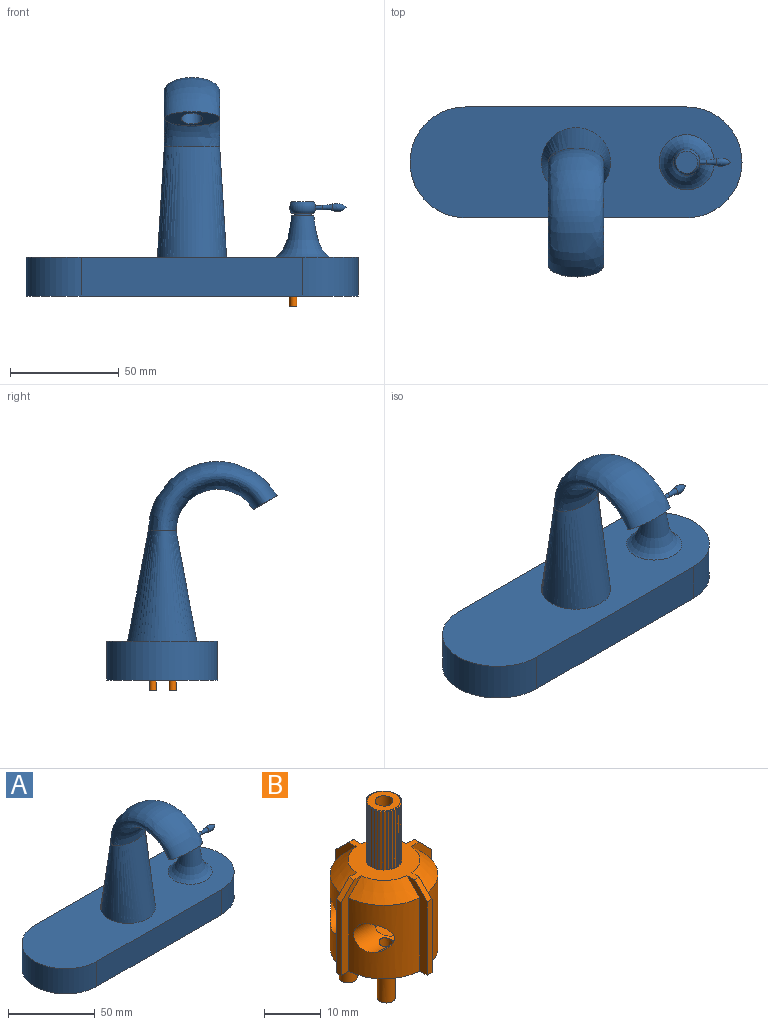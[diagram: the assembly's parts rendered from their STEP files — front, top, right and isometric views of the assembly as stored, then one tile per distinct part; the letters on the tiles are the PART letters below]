
ASSEMBLY  parts=2 mates=1
PART A: 38 faces, bbox 152.4x78.2x100.3 mm
  f0: plane 152.4x50.8mm, normal (0,0,1), area 5889.9mm2, adj f1,f2,f3,f4,f5,f13
  f1: cylinder r=25.4mm len=50.8mm, axis (0,0,-1), area 1418.8mm2, adj f0,f2,f4,f19
  f2: plane 101.6x17.78mm, normal (0,1,0), area 1806.4mm2, adj f0,f1,f3,f19
  f3: cylinder r=25.4mm len=50.8mm, axis (0,0,-1), area 1418.8mm2, adj f0,f2,f4,f19
  f4: plane 101.6x17.78mm, normal (0,-1,0), area 1806.4mm2, adj f0,f1,f3,f19
  f5: bspline ~50.8x31.75mm, area 4117.2mm2, adj f0,f7
  f6: plane 25.4x10.95mm, normal (0,-0.51,-0.86), area 180.2mm2, adj f7,f8
  f7: bspline ~59.11x31.71mm, area 4076.1mm2, adj f5,f6
  f8: cylinder r=4.83mm len=11.54mm, axis (0,-0.51,-0.86), area 192.5mm2, adj f6,f9
  f9: plane 9.65x8.32mm, normal (0,-0.51,-0.86), area 73.2mm2, adj f8
  f10: plane 10.16x10.16mm, normal (0,0,-1), area 29mm2, adj f11,f15
  f11: torus R=2.24mm, axis (0,0,1), area 197.1mm2, adj f10,f12,f16
  f12: plane 10.16x10.16mm, normal (0,0,1), area 81.1mm2, adj f11
  f13: revolved ~25.4x25.4mm, area 1006.7mm2, adj f0,f14
  f14: plane 10.16x10.16mm, normal (0,0,1), area 29mm2, adj f13,f15
  f15: cylinder r=4.07mm len=8.14mm, axis (0,0,1), area 32.5mm2, adj f10,f14
  f16: cylinder r=0.94mm len=2.97mm, axis (-1,0,0), area 17.5mm2, adj f11,f18
  f17: revolved ~6.43x3.71mm, area 59.7mm2, adj f18
  f18: torus R=18.93mm, axis (-1,0,0), area 36mm2, adj f16,f17
  f19: plane 152.4x50.8mm, normal (0,0,-1), area 6892.7mm2, adj f1,f2,f3,f4,f21,f22,f23,f24
  f20: plane 22.75x22.75mm, normal (0,0,-1), area 295.4mm2, adj f21,f22,f23,f24,f25,f26,f27,f28
  f21: plane 16.51x1.84mm, normal (0,1,0), area 30.4mm2, adj f19,f20,f22,f37
  f22: plane 16.51x1.18mm, normal (1,0,0), area 19.6mm2, adj f19,f20,f21,f23
  f23: plane 16.51x1.84mm, normal (0,-1,0), area 30.4mm2, adj f19,f20,f22,f24
  f24: cylinder r=9.55mm len=16.51mm, axis (0,0,-1), area 228.2mm2, adj f19,f20,f23,f25
  f25: plane 16.51x1.84mm, normal (1,0,0), area 30.4mm2, adj f19,f20,f24,f26
  f26: plane 16.51x1.18mm, normal (0,-1,0), area 19.6mm2, adj f19,f20,f25,f27
  f27: plane 16.51x1.84mm, normal (-1,0,0), area 30.4mm2, adj f19,f20,f26,f28
  f28: cylinder r=9.55mm len=16.51mm, axis (0,0,-1), area 228.2mm2, adj f19,f20,f27,f29
  f29: plane 16.51x1.84mm, normal (0,-1,0), area 30.4mm2, adj f19,f20,f28,f30
  f30: plane 16.51x1.17mm, normal (-1,0,0), area 19.3mm2, adj f19,f20,f29,f31
  f31: plane 16.51x0.91mm, normal (-0.02,1,0), area 15mm2, adj f19,f20,f30,f32
  f32: plane 16.51x0.93mm, normal (0,1,0), area 15.3mm2, adj f19,f20,f31,f33
  f33: cylinder r=9.55mm len=16.51mm, axis (0,0,-1), area 228.2mm2, adj f19,f20,f32,f34
  f34: plane 16.51x1.84mm, normal (-1,0,0), area 30.4mm2, adj f19,f20,f33,f35
  f35: plane 16.51x1.18mm, normal (0,1,0), area 19.6mm2, adj f19,f20,f34,f36
  f36: plane 16.51x1.84mm, normal (1,0,0), area 30.4mm2, adj f19,f20,f35,f37
  f37: cylinder r=9.55mm len=16.51mm, axis (0,0,-1), area 228.2mm2, adj f19,f20,f21,f36
PART B: 199 faces, bbox 23.2x23.2x38.6 mm
  f0: plane 3.23x3.18mm, normal (0,0,1), area 7.9mm2, adj f16
  f1: cone r=3.14mm half-angle=61.9deg, axis (0,0,1), area 0mm2, adj f32,f33,f157,f159
  f2: cone r=3.14mm half-angle=61.9deg, axis (0,0,1), area 0mm2, adj f31,f33,f153,f155
  f3: cone r=3.14mm half-angle=61.9deg, axis (0,0,1), area 0mm2, adj f30,f33,f149,f151
  f4: cone r=3.14mm half-angle=61.9deg, axis (0,0,1), area 0mm2, adj f29,f33,f145,f147
  f5: cone r=3.14mm half-angle=61.9deg, axis (0,0,1), area 0mm2, adj f28,f33,f141,f143
  f6: cone r=3.14mm half-angle=61.9deg, axis (0,0,1), area 0mm2, adj f27,f33,f137,f139
  f7: cone r=3.14mm half-angle=61.9deg, axis (0,0,1), area 0mm2, adj f26,f33,f133,f135
  f8: cone r=3.14mm half-angle=61.9deg, axis (0,0,1), area 0mm2, adj f25,f33,f129,f131
  f9: cone r=3.14mm half-angle=61.9deg, axis (0,0,1), area 0mm2, adj f24,f33,f125,f127
  f10: cone r=3.14mm half-angle=61.9deg, axis (0,0,1), area 0mm2, adj f23,f33,f121,f123
  f11: cone r=3.14mm half-angle=61.9deg, axis (0,0,1), area 0mm2, adj f22,f33,f117,f119
  f12: cone r=3.14mm half-angle=61.9deg, axis (0,0,1), area 0.1mm2, adj f21,f33,f57,f115
  f13: cone r=3.14mm half-angle=61.9deg, axis (0,0,1), area 0mm2, adj f20,f33,f53,f55
  f14: cone r=3.14mm half-angle=61.9deg, axis (0,0,1), area 0mm2, adj f19,f33,f49,f51
  f15: cone r=3.14mm half-angle=61.9deg, axis (0,0,1), area 0mm2, adj f18,f33,f45,f47
  f16: cylinder r=1.59mm len=6.35mm, axis (0,0,-1), area 63.3mm2, adj f0,f33
  f17: cone r=3.14mm half-angle=61.9deg, axis (0,0,1), area 0mm2, adj f33,f34,f43,f161
  f18: cone r=3.13mm half-angle=61.4deg, axis (0,0,-1), area 0.1mm2, adj f15,f45,f46,f47
  f19: cone r=3.13mm half-angle=61.4deg, axis (0,0,-1), area 0.1mm2, adj f14,f49,f50,f51
  f20: cone r=3.13mm half-angle=61.4deg, axis (0,0,-1), area 0.1mm2, adj f13,f53,f54,f55
  f21: cone r=3.13mm half-angle=61.4deg, axis (0,0,-1), area 2.1mm2, adj f12,f57,f58,f59,f60,f61,f62,f63
  f22: cone r=3.13mm half-angle=61.4deg, axis (0,0,-1), area 0.1mm2, adj f11,f117,f118,f119
  f23: cone r=3.13mm half-angle=61.4deg, axis (0,0,-1), area 0.1mm2, adj f10,f121,f122,f123
  f24: cone r=3.13mm half-angle=61.4deg, axis (0,0,-1), area 0.1mm2, adj f9,f125,f126,f127
  f25: cone r=3.13mm half-angle=61.4deg, axis (0,0,-1), area 0.1mm2, adj f8,f129,f130,f131
  f26: cone r=3.13mm half-angle=61.4deg, axis (0,0,-1), area 0.1mm2, adj f7,f133,f134,f135
  f27: cone r=3.13mm half-angle=61.4deg, axis (0,0,-1), area 0.1mm2, adj f6,f137,f138,f139
  f28: cone r=3.13mm half-angle=61.4deg, axis (0,0,-1), area 0.1mm2, adj f5,f141,f142,f143
  f29: cone r=3.13mm half-angle=61.4deg, axis (0,0,-1), area 0.1mm2, adj f4,f145,f146,f147
  f30: cone r=3.13mm half-angle=61.4deg, axis (0,0,-1), area 0.1mm2, adj f3,f149,f150,f151
  f31: cone r=3.13mm half-angle=61.4deg, axis (0,0,-1), area 0.1mm2, adj f2,f153,f154,f155
  f32: cone r=3.13mm half-angle=61.4deg, axis (0,0,-1), area 0.1mm2, adj f1,f157,f158,f159
  f33: plane 6.02x6.02mm, normal (0,0,1), area 19.8mm2, adj f1,f2,f3,f4,f5,f6,f7,f8
  f34: cone r=3.13mm half-angle=61.4deg, axis (0,0,-1), area 0.1mm2, adj f17,f42,f43,f161
  f35: plane 2.59x2.54mm, normal (0,0,-1), area 5.1mm2, adj f162
  f36: plane 3.23x3.18mm, normal (0,0,-1), area 2.8mm2, adj f163,f178
  f37: plane 3.18x3.18mm, normal (0.71,0,0.71), area 5.6mm2, adj f166,f167,f168,f180
  f38: cone r=7.94mm half-angle=45deg, axis (0,0,-1), area 50.3mm2, adj f168,f169,f170,f180
  f39: cone r=7.94mm half-angle=45deg, axis (0,0,-1), area 50.3mm2, adj f172,f173,f174,f180
  f40: plane 3.18x3.18mm, normal (0,-0.71,0.71), area 5.6mm2, adj f174,f175,f176,f180
  f41: cone r=7.94mm half-angle=45deg, axis (0,0,-1), area 50.3mm2, adj f166,f176,f177,f180
  f42: cylinder r=3.17mm len=12.62mm, axis (0,0,1), area 5.8mm2, adj f34,f43,f161,f180
  f43: plane 12.7x0.17mm, normal (0.81,-0.59,0), area 2.6mm2, adj f17,f33,f34,f42,f44,f180
  f44: plane 12.7x0.16mm, normal (0.59,0.81,0), area 2.6mm2, adj f33,f43,f45,f180
  f45: plane 12.7x0.17mm, normal (-0.81,0.59,0), area 2.6mm2, adj f15,f18,f33,f44,f46,f180
  f46: cylinder r=3.17mm len=12.61mm, axis (0,0,1), area 5.8mm2, adj f18,f45,f47,f180
  f47: plane 12.7x0.15mm, normal (0.67,-0.74,0), area 2.6mm2, adj f15,f18,f33,f46,f48,f180
  f48: plane 12.7x0.15mm, normal (0.74,0.67,0), area 2.6mm2, adj f33,f47,f49,f180
  f49: plane 12.7x0.16mm, normal (-0.67,0.74,0), area 2.6mm2, adj f14,f19,f33,f48,f50,f180
  f50: cylinder r=3.17mm len=12.61mm, axis (0,0,1), area 5.8mm2, adj f19,f49,f51,f180
  f51: plane 12.7x0.18mm, normal (0.5,-0.87,0), area 2.6mm2, adj f14,f19,f33,f50,f52,f180
  f52: plane 12.7x0.18mm, normal (0.87,0.5,0), area 2.6mm2, adj f33,f51,f53,f180
  f53: plane 12.7x0.18mm, normal (-0.5,0.87,0), area 2.6mm2, adj f13,f20,f33,f52,f54,f180
  f54: cylinder r=3.17mm len=12.6mm, axis (0,0,1), area 5.8mm2, adj f20,f53,f55,f180
  f55: plane 12.7x0.19mm, normal (0.31,-0.95,0), area 2.6mm2, adj f13,f20,f33,f54,f56,f180
  f56: plane 12.7x0.19mm, normal (0.95,0.31,0), area 2.6mm2, adj f33,f55,f57,f180
  f57: plane 12.7x0.2mm, normal (-0.31,0.95,0), area 2.6mm2, adj f12,f21,f33,f56,f58,f180
  f58: cylinder r=3.17mm len=12.59mm, axis (0,0,1), area 5.8mm2, adj f21,f57,f59,f180
  f59: plane 12.69x0.2mm, normal (0.1,-0.99,0), area 2.6mm2, adj f21,f58,f60,f180
  f60: plane 12.69x0.21mm, normal (0.99,0.1,0), area 2.6mm2, adj f21,f59,f61,f180
  f61: plane 12.69x0.21mm, normal (-0.1,0.99,0), area 2.6mm2, adj f21,f60,f62,f180
  f62: cylinder r=3.17mm len=12.58mm, axis (0,0,1), area 5.8mm2, adj f21,f61,f63,f180
  f63: plane 12.68x0.2mm, normal (-0.1,-0.99,0), area 2.6mm2, adj f21,f62,f64,f180
  f64: plane 12.68x0.21mm, normal (0.99,-0.1,0), area 2.6mm2, adj f21,f63,f65,f180
  f65: plane 12.68x0.21mm, normal (0.1,0.99,0), area 2.6mm2, adj f21,f64,f66,f180
  f66: cylinder r=3.17mm len=12.57mm, axis (0,0,1), area 5.8mm2, adj f21,f65,f67,f180
  f67: plane 12.67x0.19mm, normal (-0.31,-0.95,0), area 2.6mm2, adj f21,f66,f68,f180
  f68: plane 12.68x0.2mm, normal (0.95,-0.31,0), area 2.6mm2, adj f21,f67,f69,f180
  f69: plane 12.67x0.2mm, normal (0.31,0.95,0), area 2.6mm2, adj f21,f68,f70,f180
  f70: cylinder r=3.17mm len=12.56mm, axis (0,0,1), area 5.8mm2, adj f21,f69,f71,f180
  f71: plane 12.66x0.18mm, normal (-0.5,-0.87,0), area 2.6mm2, adj f21,f70,f72,f180
  f72: plane 12.67x0.18mm, normal (0.87,-0.5,0), area 2.6mm2, adj f21,f71,f73,f180
  f73: plane 12.66x0.18mm, normal (0.5,0.87,0), area 2.6mm2, adj f21,f72,f74,f180
  f74: cylinder r=3.17mm len=12.55mm, axis (0,0,1), area 5.8mm2, adj f21,f73,f75,f180
  f75: plane 12.66x0.15mm, normal (-0.67,-0.74,0), area 2.6mm2, adj f21,f74,f76,f180
  f76: plane 12.66x0.16mm, normal (0.74,-0.67,0), area 2.6mm2, adj f21,f75,f77,f180
  f77: plane 12.66x0.15mm, normal (0.67,0.74,0), area 2.6mm2, adj f21,f76,f78,f180
  f78: cylinder r=3.17mm len=12.54mm, axis (0,0,1), area 5.8mm2, adj f21,f77,f79,f180
  f79: plane 12.65x0.17mm, normal (-0.81,-0.59,0), area 2.6mm2, adj f21,f78,f80,f180
  f80: plane 12.66x0.17mm, normal (0.59,-0.81,0), area 2.6mm2, adj f21,f79,f81,f180
  f81: plane 12.65x0.17mm, normal (0.81,0.59,0), area 2.6mm2, adj f21,f80,f82,f180
  f82: cylinder r=3.17mm len=12.54mm, axis (0,0,1), area 5.8mm2, adj f21,f81,f83,f180
  f83: plane 12.65x0.19mm, normal (-0.91,-0.41,0), area 2.6mm2, adj f21,f82,f84,f180
  f84: plane 12.66x0.19mm, normal (0.41,-0.91,0), area 2.6mm2, adj f21,f83,f85,f180
  f85: plane 12.65x0.19mm, normal (0.91,0.41,0), area 2.6mm2, adj f21,f84,f86,f180
  f86: cylinder r=3.17mm len=12.54mm, axis (0,0,1), area 5.8mm2, adj f21,f85,f87,f180
  f87: plane 12.65x0.2mm, normal (-0.98,-0.21,0), area 2.6mm2, adj f21,f86,f88,f180
  f88: plane 12.66x0.2mm, normal (0.21,-0.98,0), area 2.6mm2, adj f21,f87,f89,f180
  f89: plane 12.65x0.2mm, normal (0.98,0.21,0), area 2.6mm2, adj f21,f88,f90,f180
  f90: cylinder r=3.17mm len=12.54mm, axis (0,0,1), area 5.8mm2, adj f21,f89,f91,f180
  f91: plane 12.65x0.2mm, normal (-1,0,0), area 2.6mm2, adj f21,f90,f92,f180
  f92: plane 12.66x0.21mm, normal (0,-1,0), area 2.6mm2, adj f21,f91,f93,f180
  f93: plane 12.65x0.21mm, normal (1,0,0), area 2.6mm2, adj f21,f92,f94,f180
  f94: cylinder r=3.17mm len=12.54mm, axis (0,0,1), area 5.8mm2, adj f21,f93,f95,f180
  f95: plane 12.66x0.2mm, normal (-0.98,0.21,0), area 2.6mm2, adj f21,f94,f96,f180
  f96: plane 12.66x0.2mm, normal (-0.21,-0.98,0), area 2.6mm2, adj f21,f95,f97,f180
  f97: plane 12.66x0.2mm, normal (0.98,-0.21,0), area 2.6mm2, adj f21,f96,f98,f180
  f98: cylinder r=3.17mm len=12.55mm, axis (0,0,1), area 5.8mm2, adj f21,f97,f99,f180
  f99: plane 12.67x0.19mm, normal (-0.91,0.41,0), area 2.6mm2, adj f21,f98,f100,f180
  f100: plane 12.67x0.19mm, normal (-0.41,-0.91,0), area 2.6mm2, adj f21,f99,f101,f180
  f101: plane 12.66x0.19mm, normal (0.91,-0.41,0), area 2.6mm2, adj f21,f100,f102,f180
  f102: cylinder r=3.17mm len=12.56mm, axis (0,0,1), area 5.8mm2, adj f21,f101,f103,f180
  f103: plane 12.67x0.17mm, normal (-0.81,0.59,0), area 2.6mm2, adj f21,f102,f104,f180
  f104: plane 12.68x0.17mm, normal (-0.59,-0.81,0), area 2.6mm2, adj f21,f103,f105,f180
  f105: plane 12.67x0.17mm, normal (0.81,-0.59,0), area 2.6mm2, adj f21,f104,f106,f180
  f106: cylinder r=3.17mm len=12.57mm, axis (0,0,1), area 5.8mm2, adj f21,f105,f107,f180
  f107: plane 12.68x0.16mm, normal (-0.67,0.74,0), area 2.6mm2, adj f21,f106,f108,f180
  f108: plane 12.68x0.16mm, normal (-0.74,-0.67,0), area 2.6mm2, adj f21,f107,f109,f180
  f109: plane 12.68x0.15mm, normal (0.67,-0.74,0), area 2.6mm2, adj f21,f108,f110,f180
  f110: cylinder r=3.17mm len=12.58mm, axis (0,0,1), area 5.8mm2, adj f21,f109,f111,f180
  f111: plane 12.69x0.18mm, normal (-0.5,0.87,0), area 2.6mm2, adj f21,f110,f112,f180
  f112: plane 12.69x0.18mm, normal (-0.87,-0.5,0), area 2.6mm2, adj f21,f111,f113,f180
  f113: plane 12.69x0.18mm, normal (0.5,-0.87,0), area 2.6mm2, adj f21,f112,f114,f180
  f114: cylinder r=3.17mm len=12.59mm, axis (0,0,1), area 5.8mm2, adj f21,f113,f115,f180
  f115: plane 12.7x0.2mm, normal (-0.31,0.95,0), area 2.6mm2, adj f12,f21,f33,f114,f116,f180
  f116: plane 12.7x0.19mm, normal (-0.95,-0.31,0), area 2.6mm2, adj f33,f115,f117,f180
  f117: plane 12.7x0.2mm, normal (0.31,-0.95,0), area 2.6mm2, adj f11,f22,f33,f116,f118,f180
  f118: cylinder r=3.17mm len=12.6mm, axis (0,0,1), area 5.8mm2, adj f22,f117,f119,f180
  f119: plane 12.7x0.21mm, normal (-0.1,0.99,0), area 2.6mm2, adj f11,f22,f33,f118,f120,f180
  f120: plane 12.7x0.2mm, normal (-0.99,-0.1,0), area 2.6mm2, adj f33,f119,f121,f180
  f121: plane 12.7x0.2mm, normal (0.1,-0.99,0), area 2.6mm2, adj f10,f23,f33,f120,f122,f180
  f122: cylinder r=3.17mm len=12.61mm, axis (0,0,1), area 5.8mm2, adj f23,f121,f123,f180
  f123: plane 12.7x0.21mm, normal (0.1,0.99,0), area 2.6mm2, adj f10,f23,f33,f122,f124,f180
  f124: plane 12.7x0.2mm, normal (-0.99,0.1,0), area 2.6mm2, adj f33,f123,f125,f180
  f125: plane 12.7x0.2mm, normal (-0.1,-0.99,0), area 2.6mm2, adj f9,f24,f33,f124,f126,f180
  f126: cylinder r=3.17mm len=12.61mm, axis (0,0,1), area 5.8mm2, adj f24,f125,f127,f180
  f127: plane 12.7x0.2mm, normal (0.31,0.95,0), area 2.6mm2, adj f9,f24,f33,f126,f128,f180
  f128: plane 12.7x0.19mm, normal (-0.95,0.31,0), area 2.6mm2, adj f33,f127,f129,f180
  f129: plane 12.7x0.2mm, normal (-0.31,-0.95,0), area 2.6mm2, adj f8,f25,f33,f128,f130,f180
  f130: cylinder r=3.17mm len=12.62mm, axis (0,0,1), area 5.8mm2, adj f25,f129,f131,f180
  f131: plane 12.7x0.18mm, normal (0.5,0.87,0), area 2.6mm2, adj f8,f25,f33,f130,f132,f180
  f132: plane 12.7x0.18mm, normal (-0.87,0.5,0), area 2.6mm2, adj f33,f131,f133,f180
  f133: plane 12.7x0.18mm, normal (-0.5,-0.87,0), area 2.6mm2, adj f7,f26,f33,f132,f134,f180
  f134: cylinder r=3.17mm len=12.63mm, axis (0,0,1), area 5.8mm2, adj f26,f133,f135,f180
  f135: plane 12.7x0.15mm, normal (0.67,0.74,0), area 2.6mm2, adj f7,f26,f33,f134,f136,f180
  f136: plane 12.7x0.15mm, normal (-0.74,0.67,0), area 2.6mm2, adj f33,f135,f137,f180
  f137: plane 12.7x0.15mm, normal (-0.67,-0.74,0), area 2.6mm2, adj f6,f27,f33,f136,f138,f180
  f138: cylinder r=3.17mm len=12.63mm, axis (0,0,1), area 5.8mm2, adj f27,f137,f139,f180
  f139: plane 12.7x0.17mm, normal (0.81,0.59,0), area 2.6mm2, adj f6,f27,f33,f138,f140,f180
  f140: plane 12.7x0.16mm, normal (-0.59,0.81,0), area 2.6mm2, adj f33,f139,f141,f180
  f141: plane 12.7x0.17mm, normal (-0.81,-0.59,0), area 2.6mm2, adj f5,f28,f33,f140,f142,f180
  f142: cylinder r=3.17mm len=12.64mm, axis (0,0,1), area 5.8mm2, adj f28,f141,f143,f180
  f143: plane 12.7x0.19mm, normal (0.91,0.41,0), area 2.6mm2, adj f5,f28,f33,f142,f144,f180
  f144: plane 12.7x0.19mm, normal (-0.41,0.91,0), area 2.6mm2, adj f33,f143,f145,f180
  f145: plane 12.7x0.19mm, normal (-0.91,-0.41,0), area 2.6mm2, adj f4,f29,f33,f144,f146,f180
  f146: cylinder r=3.17mm len=12.64mm, axis (0,0,1), area 5.8mm2, adj f29,f145,f147,f180
  f147: plane 12.7x0.2mm, normal (0.98,0.21,0), area 2.6mm2, adj f4,f29,f33,f146,f148,f180
  f148: plane 12.7x0.2mm, normal (-0.21,0.98,0), area 2.6mm2, adj f33,f147,f149,f180
  f149: plane 12.7x0.2mm, normal (-0.98,-0.21,0), area 2.6mm2, adj f3,f30,f33,f148,f150,f180
  f150: cylinder r=3.17mm len=12.64mm, axis (0,0,1), area 5.8mm2, adj f30,f149,f151,f180
  f151: plane 12.7x0.2mm, normal (1,0,0), area 2.6mm2, adj f3,f30,f33,f150,f152,f180
  f152: plane 12.7x0.2mm, normal (0,1,0), area 2.6mm2, adj f33,f151,f153,f180
  f153: plane 12.7x0.21mm, normal (-1,0,0), area 2.6mm2, adj f2,f31,f33,f152,f154,f180
  f154: cylinder r=3.17mm len=12.63mm, axis (0,0,1), area 5.8mm2, adj f31,f153,f155,f180
  f155: plane 12.7x0.2mm, normal (0.98,-0.21,0), area 2.6mm2, adj f2,f31,f33,f154,f156,f180
  f156: plane 12.7x0.2mm, normal (0.21,0.98,0), area 2.6mm2, adj f33,f155,f157,f180
  f157: plane 12.7x0.2mm, normal (-0.98,0.21,0), area 2.6mm2, adj f1,f32,f33,f156,f158,f180
  f158: cylinder r=3.17mm len=12.63mm, axis (0,0,1), area 5.8mm2, adj f32,f157,f159,f180
  f159: plane 12.7x0.19mm, normal (0.91,-0.41,0), area 2.6mm2, adj f1,f32,f33,f158,f160,f180
  f160: plane 12.7x0.19mm, normal (0.41,0.91,0), area 2.6mm2, adj f33,f159,f161,f180
  f161: plane 12.7x0.19mm, normal (-0.91,0.41,0), area 2.6mm2, adj f17,f33,f34,f42,f160,f180
  f162: cylinder r=1.27mm len=2.54mm, axis (0,0,1), area 9.3mm2, adj f35,f186
  f163: cylinder r=1.27mm len=12.13mm, axis (0,0,1), area 95.9mm2, adj f36,f186
  f164: plane 3.18x3.18mm, normal (0,0.71,0.71), area 5.6mm2, adj f170,f171,f180,f188
  f165: cylinder r=1.59mm len=3.18mm, axis (0,0,1), area 15.8mm2, adj f183,f189
  f166: plane 19.51x5.49mm, normal (0,-1,0), area 35.3mm2, adj f37,f41,f167,f177,f180,f189
  f167: plane 15.88x1.24mm, normal (1,0,0), area 19.7mm2, adj f37,f166,f168,f189
  f168: plane 19.51x5.5mm, normal (0,1,0), area 35.4mm2, adj f37,f38,f167,f169,f180,f189
  f169: cylinder r=9.53mm len=15.88mm, axis (0,0,1), area 217.8mm2, adj f38,f168,f170,f189
  f170: plane 19.51x5.49mm, normal (1,0,0), area 35.3mm2, adj f38,f164,f169,f171,f180,f189
  f171: plane 15.88x1.24mm, normal (0,1,0), area 19.7mm2, adj f164,f170,f188,f189
  f172: plane 19.51x5.5mm, normal (0,-1,0), area 35.4mm2, adj f39,f173,f179,f180,f181,f189
  f173: cylinder r=9.53mm len=15.88mm, axis (0,0,1), area 180.7mm2, adj f39,f172,f174,f186,f189
  f174: plane 19.51x5.49mm, normal (-1,0,0), area 35.3mm2, adj f39,f40,f173,f175,f180,f189
  f175: plane 15.88x1.24mm, normal (0,-1,0), area 19.7mm2, adj f40,f174,f176,f189
  f176: plane 19.51x5.5mm, normal (1,0,0), area 35.4mm2, adj f40,f41,f175,f177,f180,f189
  f177: cylinder r=9.53mm len=15.88mm, axis (0,0,1), area 217.8mm2, adj f41,f166,f176,f189
  f178: cylinder r=1.59mm len=6.35mm, axis (0,0,-1), area 63.3mm2, adj f36,f189
  f179: plane 3.18x3.18mm, normal (-0.71,0,0.71), area 5.6mm2, adj f172,f180,f181,f190
  f180: plane 16.37x16.37mm, normal (0,0,1), area 105.4mm2, adj f37,f38,f39,f40,f41,f42,f43,f44
  f181: plane 15.88x1.24mm, normal (-1,0,0), area 19.7mm2, adj f172,f179,f189,f190
  f182: plane 2.53x2.48mm, normal (0,0,-1), area 4.8mm2, adj f192
  f183: plane 9.37x9.2mm, normal (0,0,1), area 58.6mm2, adj f165,f193
  f184: plane 9.37x9.2mm, normal (0,0,-1), area 66.5mm2, adj f193
  f185: plane 6.18x3.53mm, normal (-1,0,0), area 17.4mm2, adj f186,f193
  f186: cylinder r=3.06mm len=10.7mm, axis (1,0,0), area 123.1mm2, adj f162,f163,f173,f185,f193
  f187: cone r=7.94mm half-angle=45deg, axis (0,0,-1), area 50.3mm2, adj f180,f188,f190,f194
  f188: plane 19.51x5.5mm, normal (-1,0,0), area 35.4mm2, adj f164,f171,f180,f187,f189,f194
  f189: plane 22.72x22.72mm, normal (0,0,-1), area 270.4mm2, adj f165,f166,f167,f168,f169,f170,f171,f172
  f190: plane 19.51x5.49mm, normal (0,1,0), area 35.3mm2, adj f179,f180,f181,f187,f189,f194
  f191: cylinder r=1.59mm len=6.35mm, axis (0,0,-1), area 63.3mm2, adj f189,f196
  f192: cylinder r=1.24mm len=2.48mm, axis (0,0,1), area 10.1mm2, adj f182,f197
  f193: cylinder r=4.6mm len=11.11mm, axis (0,0,1), area 262.9mm2, adj f183,f184,f185,f186,f195,f197
  f194: cylinder r=9.53mm len=15.88mm, axis (0,0,1), area 181mm2, adj f187,f188,f189,f190,f197
  f195: plane 6.15x3.44mm, normal (-1,0,0), area 17mm2, adj f193,f197
  f196: plane 3.23x3.18mm, normal (0,0,-1), area 3.1mm2, adj f191,f198
  f197: cylinder r=3.06mm len=10.71mm, axis (1,0,0), area 121.7mm2, adj f192,f193,f194,f195,f198
  f198: cylinder r=1.24mm len=12.37mm, axis (0,0,1), area 94.8mm2, adj f196,f197
PLACE A t=(6.33,13.65,0)mm
PLACE B t=(57.13,13.65,-3.56)mm
MATE slider B.f16 <-> A.f24  axis (0,0,1) through (57.13,13.65,-3.56)mm
